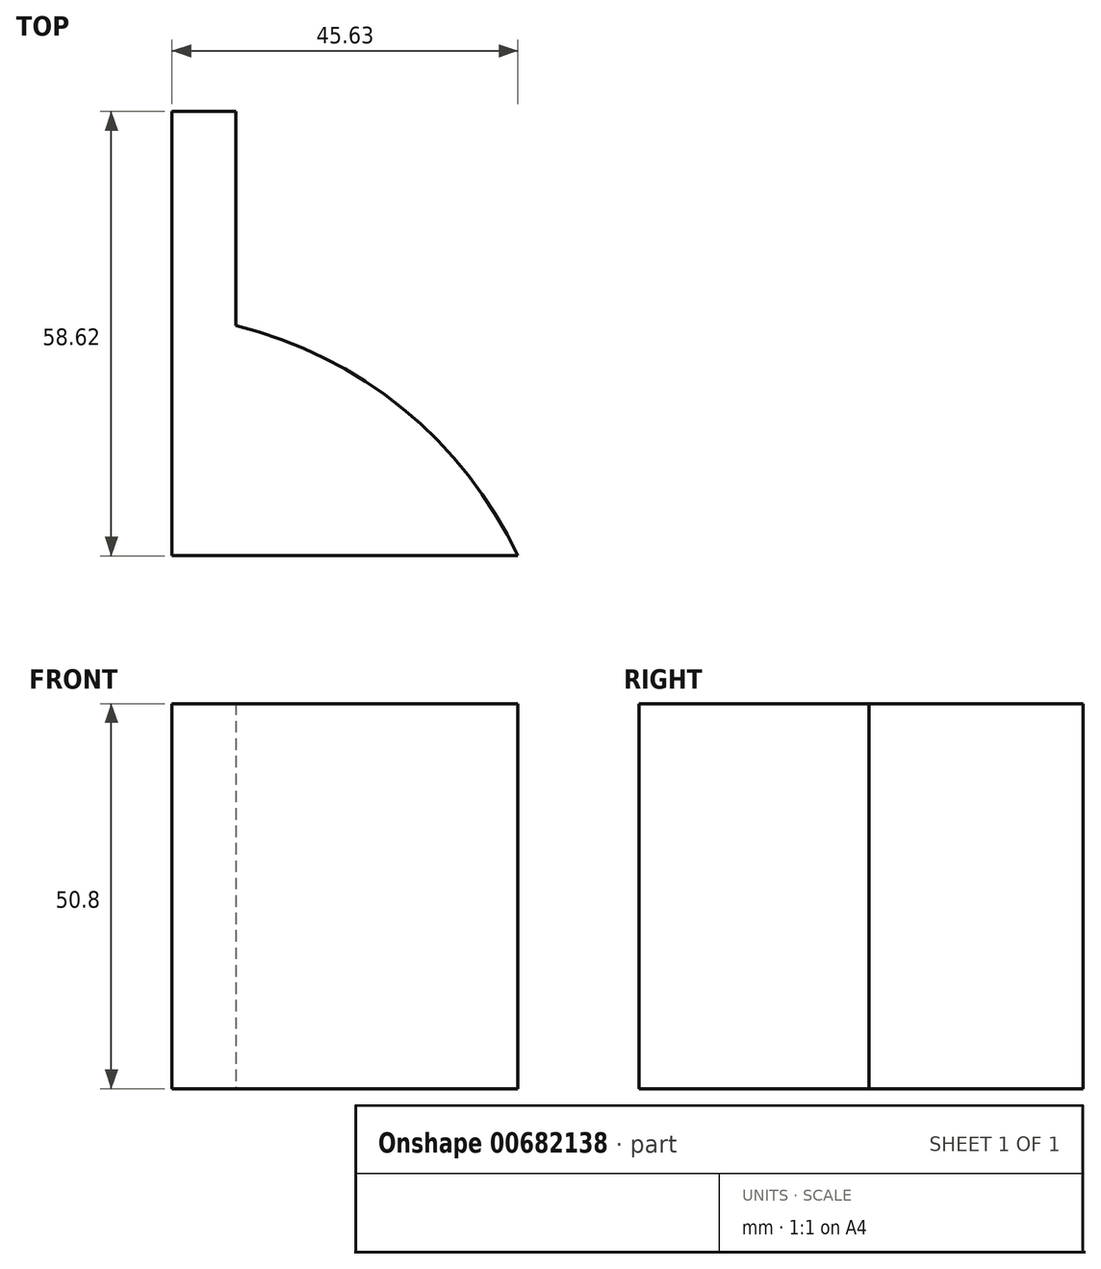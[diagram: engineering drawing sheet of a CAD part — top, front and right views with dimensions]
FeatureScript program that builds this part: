
annotation { "Feature Type Name" : "Feature", "Feature Type Description" : "" }
export const myFeature = defineFeature(function(context is Context, id is Id, definition is map)
    precondition{}
    {
        {
            var Q0;
            Q0=qCreatedBy(makeId("Top.planeOp"),FACE);
            var sketch = newSketch(context, id + "F0", { "sketchPlane" : qUnion([Q0])});
            skLineSegment(sketch, "E0", {"start": v(-47.83, 36) * mm, "end": v(-47.83, -22.63) * mm});
            skLineSegment(sketch, "E1", {"start": v(-47.83, -22.63) * mm, "end": v(-2.2, -22.63) * mm});
            skLineSegment(sketch, "E2", {"start": v(-47.83, 36) * mm, "end": v(-39.43, 36) * mm});
            skLineSegment(sketch, "E3", {"start": v(-39.43, 36) * mm, "end": v(-39.43, 7.73) * mm});
            skArc(sketch, "E4", {"start": v(-2.2, -22.63) * mm, "mid": v(-17.36, -3.21) * mm, "end": v(-39.43, 7.73) * mm});
            skSolve(sketch);
        }
        {
            var Q0;
            Q0 = qSketchRegion(id + "F0", true);
            extrude(context, id + "F1", {"entities" : qUnion([Q0]), "depth" : 50.8 * mm, "offsetDistance" : 25.4 * mm});
        }
    });
